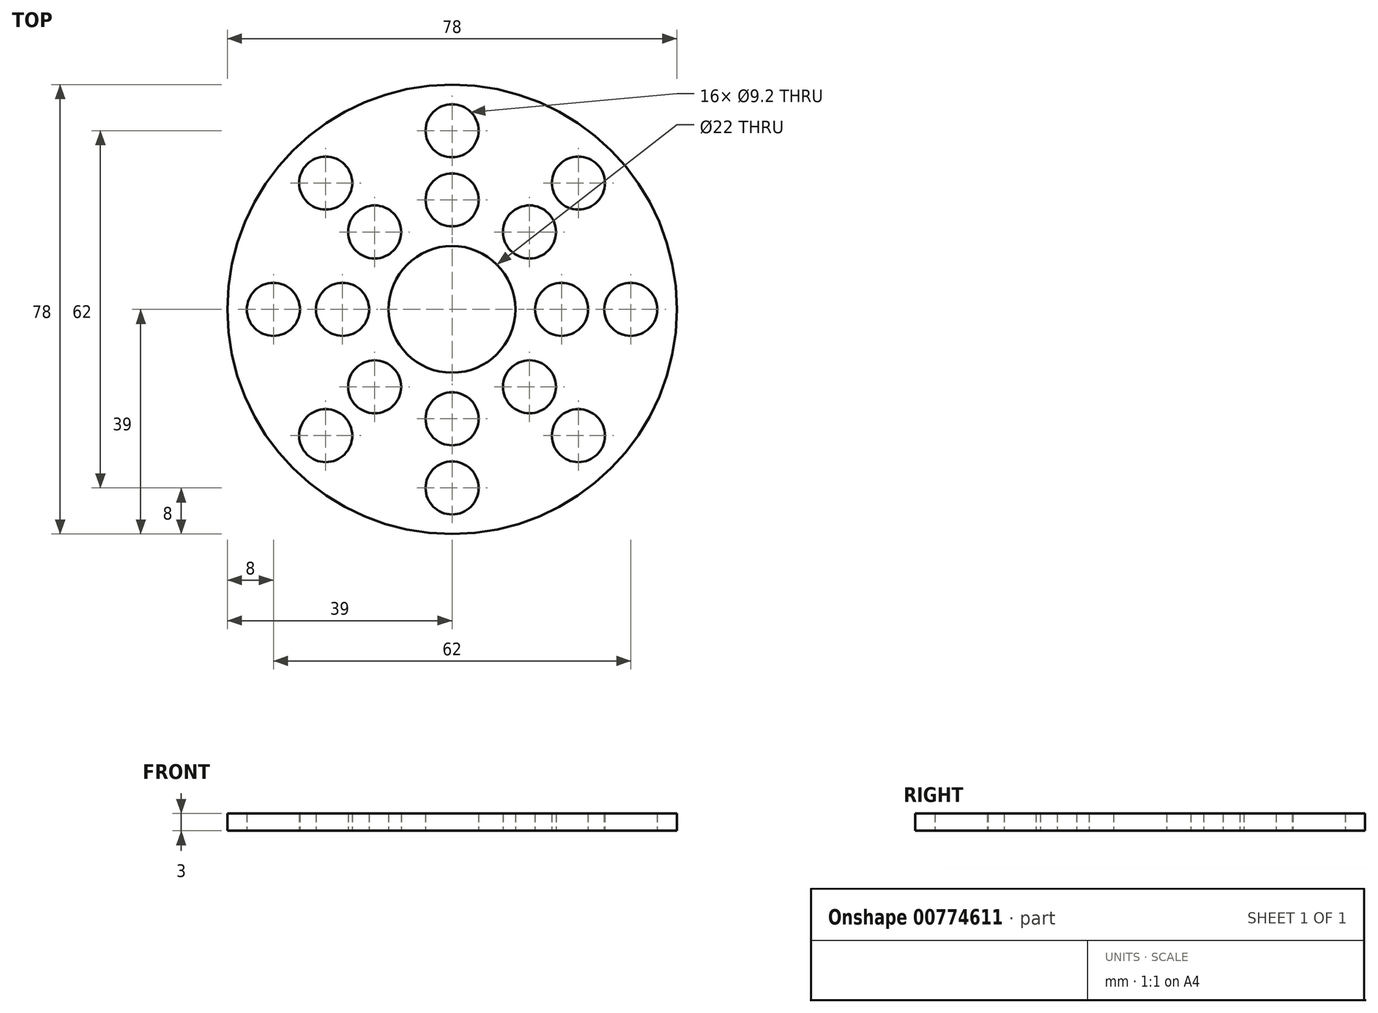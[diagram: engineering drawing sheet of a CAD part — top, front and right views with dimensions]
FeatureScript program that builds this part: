
annotation { "Feature Type Name" : "Feature", "Feature Type Description" : "" }
export const myFeature = defineFeature(function(context is Context, id is Id, definition is map)
    precondition{}
    {
        {
            var Q0;
            Q0=qCreatedBy(makeId("Top.planeOp"),FACE);
            var sketch = newSketch(context, id + "F0", { "sketchPlane" : qUnion([Q0])});
            skCircle(sketch, "E0", {"center": v(0, 0) * mm, "radius": 11 * mm});
            skCircle(sketch, "E1", {"center": v(0, 0) * mm, "radius": 39 * mm});
            skLineSegment(sketch, "E2", {"start": v(0, 0) * mm, "end": v(0, 31) * mm});
            skCircle(sketch, "E3", {"center": v(0, 31) * mm, "radius": 4.6 * mm});
            skCircle(sketch, "E4", {"center": v(0, 19) * mm, "radius": 4.6 * mm});
            skLineSegment(sketch, "E5", {"start": v(0, 0) * mm, "end": v(0, 19) * mm});
            skCircle(sketch, "E6.1.0", {"center": v(-13.44, 13.44) * mm, "radius": 4.6 * mm});
            skCircle(sketch, "E6.1.1", {"center": v(-21.92, 21.92) * mm, "radius": 4.6 * mm});
            skCircle(sketch, "E6.2.0", {"center": v(-19, 0) * mm, "radius": 4.6 * mm});
            skCircle(sketch, "E6.2.1", {"center": v(-31, 0) * mm, "radius": 4.6 * mm});
            skCircle(sketch, "E6.3.0", {"center": v(-13.44, -13.44) * mm, "radius": 4.6 * mm});
            skCircle(sketch, "E6.3.1", {"center": v(-21.92, -21.92) * mm, "radius": 4.6 * mm});
            skCircle(sketch, "E6.4.0", {"center": v(0, -19) * mm, "radius": 4.6 * mm});
            skCircle(sketch, "E6.4.1", {"center": v(0, -31) * mm, "radius": 4.6 * mm});
            skCircle(sketch, "E6.5.0", {"center": v(13.44, -13.44) * mm, "radius": 4.6 * mm});
            skCircle(sketch, "E6.5.1", {"center": v(21.92, -21.92) * mm, "radius": 4.6 * mm});
            skCircle(sketch, "E6.6.0", {"center": v(19, 0) * mm, "radius": 4.6 * mm});
            skCircle(sketch, "E6.6.1", {"center": v(31, 0) * mm, "radius": 4.6 * mm});
            skCircle(sketch, "E6.7.0", {"center": v(13.44, 13.44) * mm, "radius": 4.6 * mm});
            skCircle(sketch, "E6.7.1", {"center": v(21.92, 21.92) * mm, "radius": 4.6 * mm});
            skSolve(sketch);
        }
        {
            var Q0;
            Q0 = qSketchRegion(id + "F0", true);
            extrude(context, id + "F1", {"entities" : qUnion([Q0]), "depth" : 3 * mm, "offsetDistance" : 25 * mm});
        }
    });
